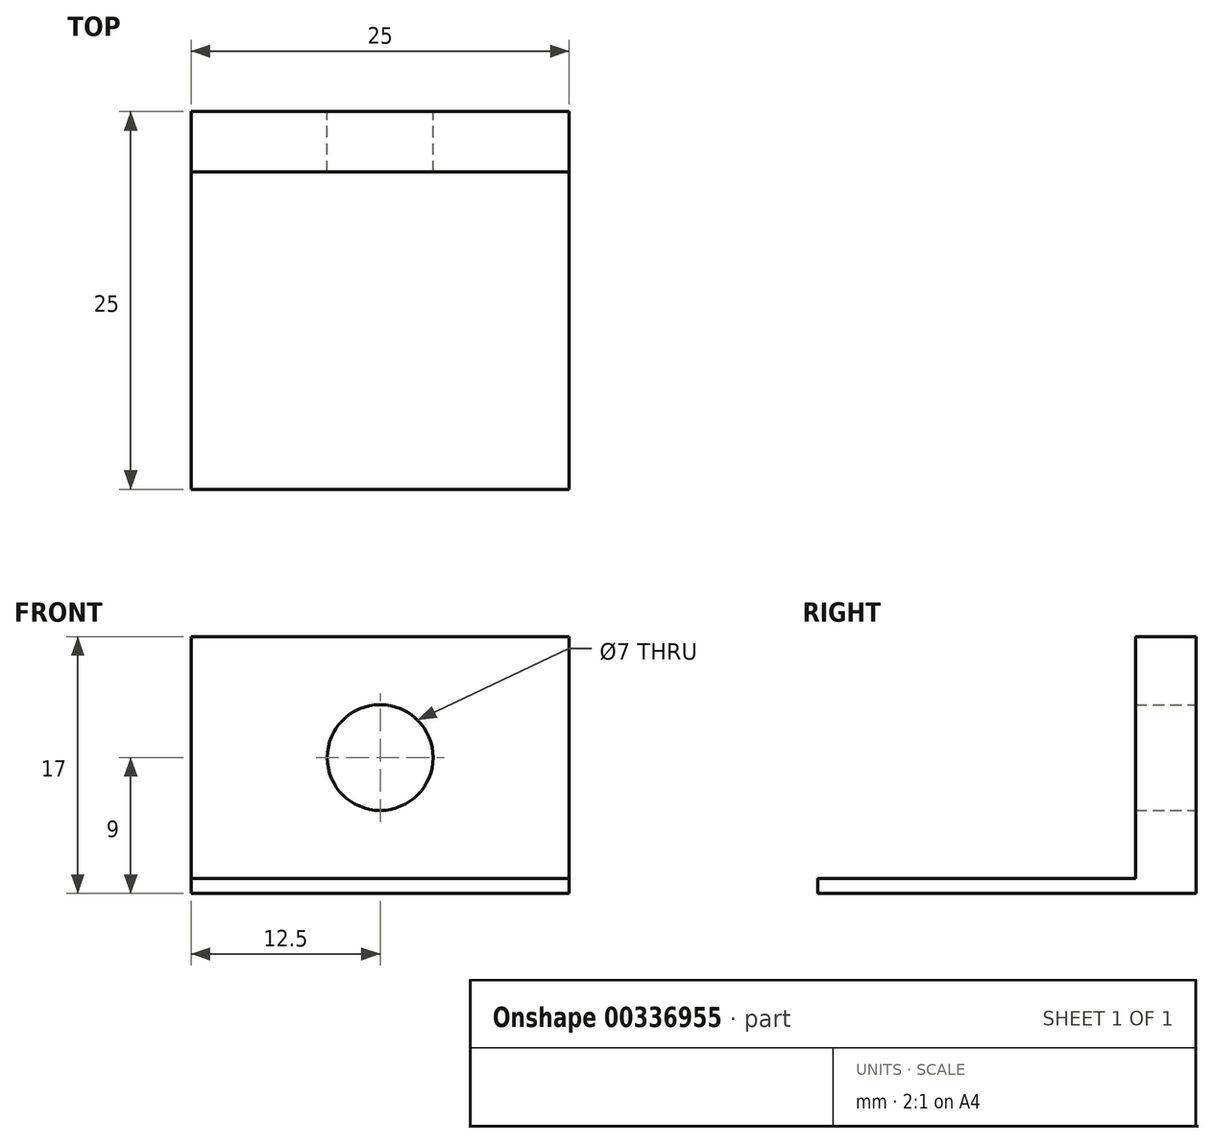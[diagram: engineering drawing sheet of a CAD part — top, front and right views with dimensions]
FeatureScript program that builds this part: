
annotation { "Feature Type Name" : "Feature", "Feature Type Description" : "" }
export const myFeature = defineFeature(function(context is Context, id is Id, definition is map)
    precondition{}
    {
        {
            var Q0;
            Q0=qCreatedBy(makeId("Top.planeOp"),FACE);
            var sketch = newSketch(context, id + "F0", { "sketchPlane" : qUnion([Q0])});
            skLineSegment(sketch, "E0.bottom", {"start": v(12.5, 12.5) * mm, "end": v(-12.5, 12.5) * mm});
            skLineSegment(sketch, "E0.top", {"start": v(12.5, -12.5) * mm, "end": v(-12.5, -12.5) * mm});
            skLineSegment(sketch, "E0.left", {"start": v(12.5, 12.5) * mm, "end": v(12.5, -12.5) * mm});
            skLineSegment(sketch, "E0.right", {"start": v(-12.5, 12.5) * mm, "end": v(-12.5, -12.5) * mm});
            skPoint(sketch, "E0.middle", {"position": v(0, 0) * mm});
            skSolve(sketch);
        }
        {
            var Q0;
            Q0=makeQuery(id+"F0.imprint","IMPRINT",FACE,{"disambiguationData":[TD([[makeQuery(id+"F0.imprint","IMPRINT",EDGE,{"derivedFrom":sQuery(id+"F0.wireOp",EDGE,"E0.bottom")}),1.0]])]});
            extrude(context, id + "F1", {"entities" : qUnion([Q0]), "depth" : 17 * mm});
        }
        {
            var Q0;
            Q0=makeQuery(id+"F1.opExtrude","CAP_FACE",FACE,{"disambiguationData":[OSD([sQuery(id+"F0.wireOp",EDGE,"E0.bottom"),sQuery(id+"F0.wireOp",EDGE,"E0.top"),sQuery(id+"F0.wireOp",EDGE,"E0.left"),sQuery(id+"F0.wireOp",EDGE,"E0.right")])],"isStart":false});
            var sketch = newSketch(context, id + "F2", { "sketchPlane" : qUnion([Q0])});
            skLineSegment(sketch, "E1", {"start": v(0, -12.5) * mm, "end": v(-12.5, -12.5) * mm});
            skLineSegment(sketch, "E2", {"start": v(-12.5, -12.5) * mm, "end": v(-12.5, 8.5) * mm});
            skLineSegment(sketch, "E3", {"start": v(-12.5, 8.5) * mm, "end": v(12.5, 8.5) * mm});
            skLineSegment(sketch, "E4", {"start": v(12.5, 8.5) * mm, "end": v(12.5, -12.5) * mm});
            skLineSegment(sketch, "E5", {"start": v(12.5, -12.5) * mm, "end": v(0, -12.5) * mm});
            skSolve(sketch);
        }
        {
            var Q0;
            Q0=makeQuery(id+"F2.imprint","IMPRINT",FACE,{"disambiguationData":[TD([[makeQuery(id+"F2.imprint","IMPRINT",EDGE,{"derivedFrom":sQuery(id+"F2.wireOp",EDGE,"E1")}),-1.0]])]});
            extrude(context, id + "F3", {"entities" : qUnion([Q0]), "operationType" : NewBodyOperationType.REMOVE, "oppositeDirection" : true, "depth" : 16 * mm});
        }
        {
            var Q0;
            Q0=makeQuery(id+"F1.opExtrude","SWEPT_FACE",FACE,{"disambiguationData":[OSD([sQuery(id+"F0.wireOp",EDGE,"E0.bottom")])]});
            var sketch = newSketch(context, id + "F4", { "sketchPlane" : qUnion([Q0])});
            skCircle(sketch, "E6", {"center": v(0, 9) * mm, "radius": 3.5 * mm});
            skSolve(sketch);
        }
        {
            var Q0;
            Q0=makeQuery(id+"F4.imprint","IMPRINT",FACE,{"disambiguationData":[TD([[makeQuery(id+"F4.imprint","IMPRINT",EDGE,{"derivedFrom":sQuery(id+"F4.wireOp",EDGE,"E6")}),1.0]])]});
            extrude(context, id + "F5", {"entities" : qUnion([Q0]), "operationType" : NewBodyOperationType.REMOVE, "endBound" : BoundingType.UP_TO_NEXT, "oppositeDirection" : true, "depth" : 25 * mm});
        }
    });
